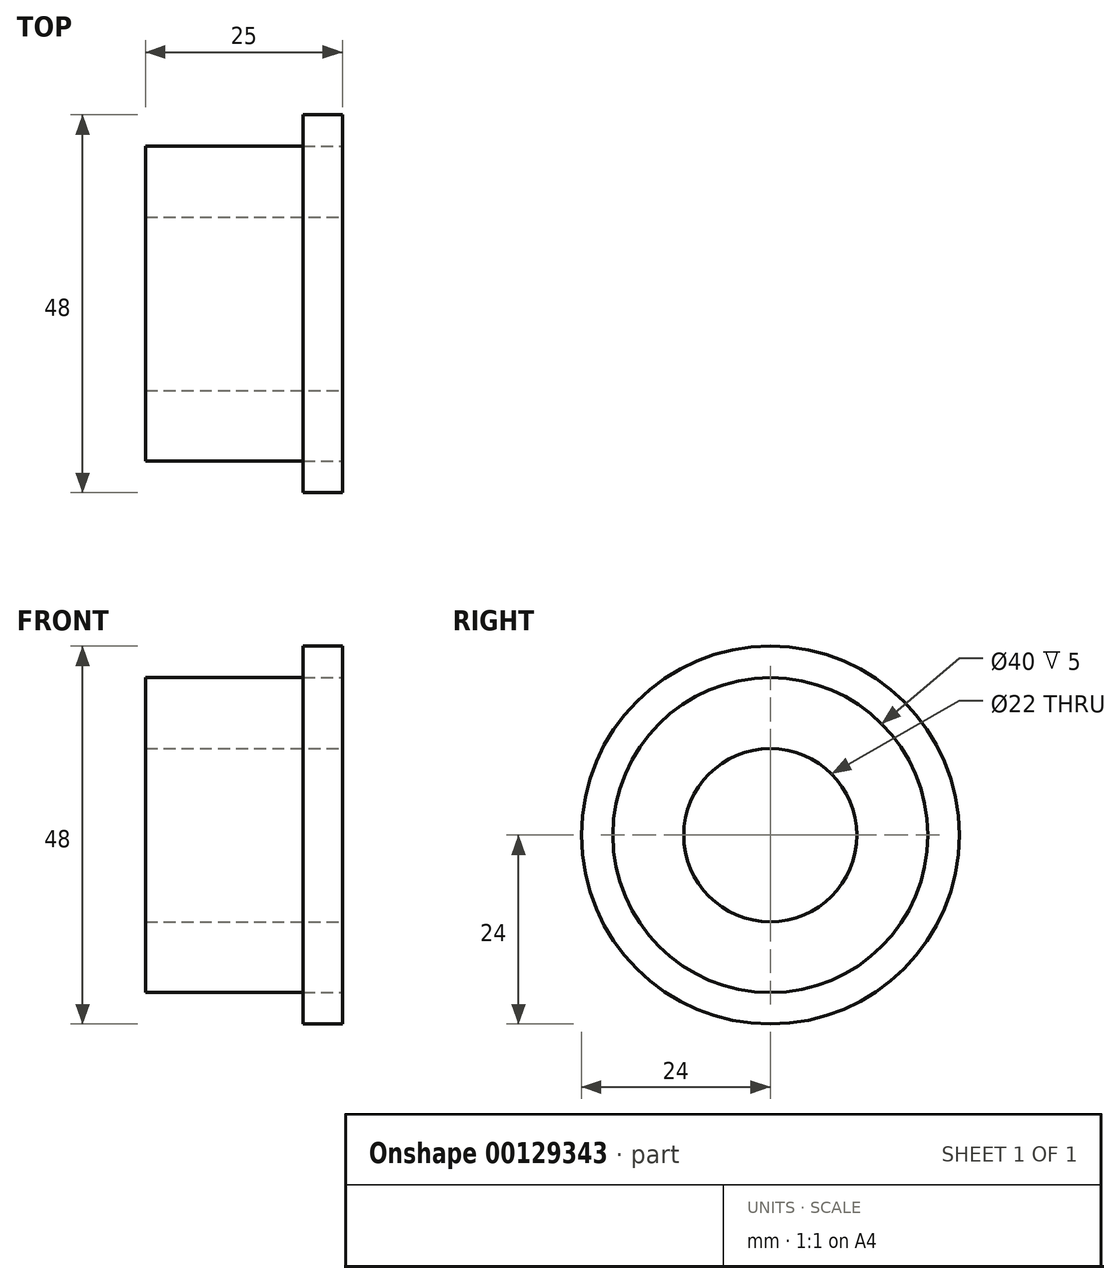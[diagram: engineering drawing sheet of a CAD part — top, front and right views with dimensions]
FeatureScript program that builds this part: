
annotation { "Feature Type Name" : "Feature", "Feature Type Description" : "" }
export const myFeature = defineFeature(function(context is Context, id is Id, definition is map)
    precondition{}
    {
        {
            var Q0;
            Q0=qCreatedBy(makeId("Right.planeOp"),FACE);
            var sketch = newSketch(context, id + "F0", { "sketchPlane" : qUnion([Q0])});
            skCircle(sketch, "E0", {"center": v(0, 0) * mm, "radius": 20 * mm});
            skCircle(sketch, "E1", {"center": v(0, 0) * mm, "radius": 11 * mm});
            skCircle(sketch, "E2", {"center": v(0, 0) * mm, "radius": 24 * mm});
            skSolve(sketch);
        }
        {
            var Q0;
            Q0=makeQuery(id+"F0.imprint","IMPRINT",FACE,{"disambiguationData":[TD([[makeQuery(id+"F0.imprint","IMPRINT",EDGE,{"derivedFrom":sQuery(id+"F0.wireOp",EDGE,"E0")}),1.0]])]});
            extrude(context, id + "F1", {"entities" : qUnion([Q0]), "oppositeDirection" : true, "depth" : 25 * mm});
        }
        {
            var Q0;
            Q0=makeQuery(id+"F0.imprint","IMPRINT",FACE,{"disambiguationData":[TD([[makeQuery(id+"F0.imprint","IMPRINT",EDGE,{"derivedFrom":sQuery(id+"F0.wireOp",EDGE,"E0")}),-1.0]])]});
            extrude(context, id + "F2", {"entities" : qUnion([Q0]), "oppositeDirection" : true, "depth" : 5 * mm});
        }
    });
